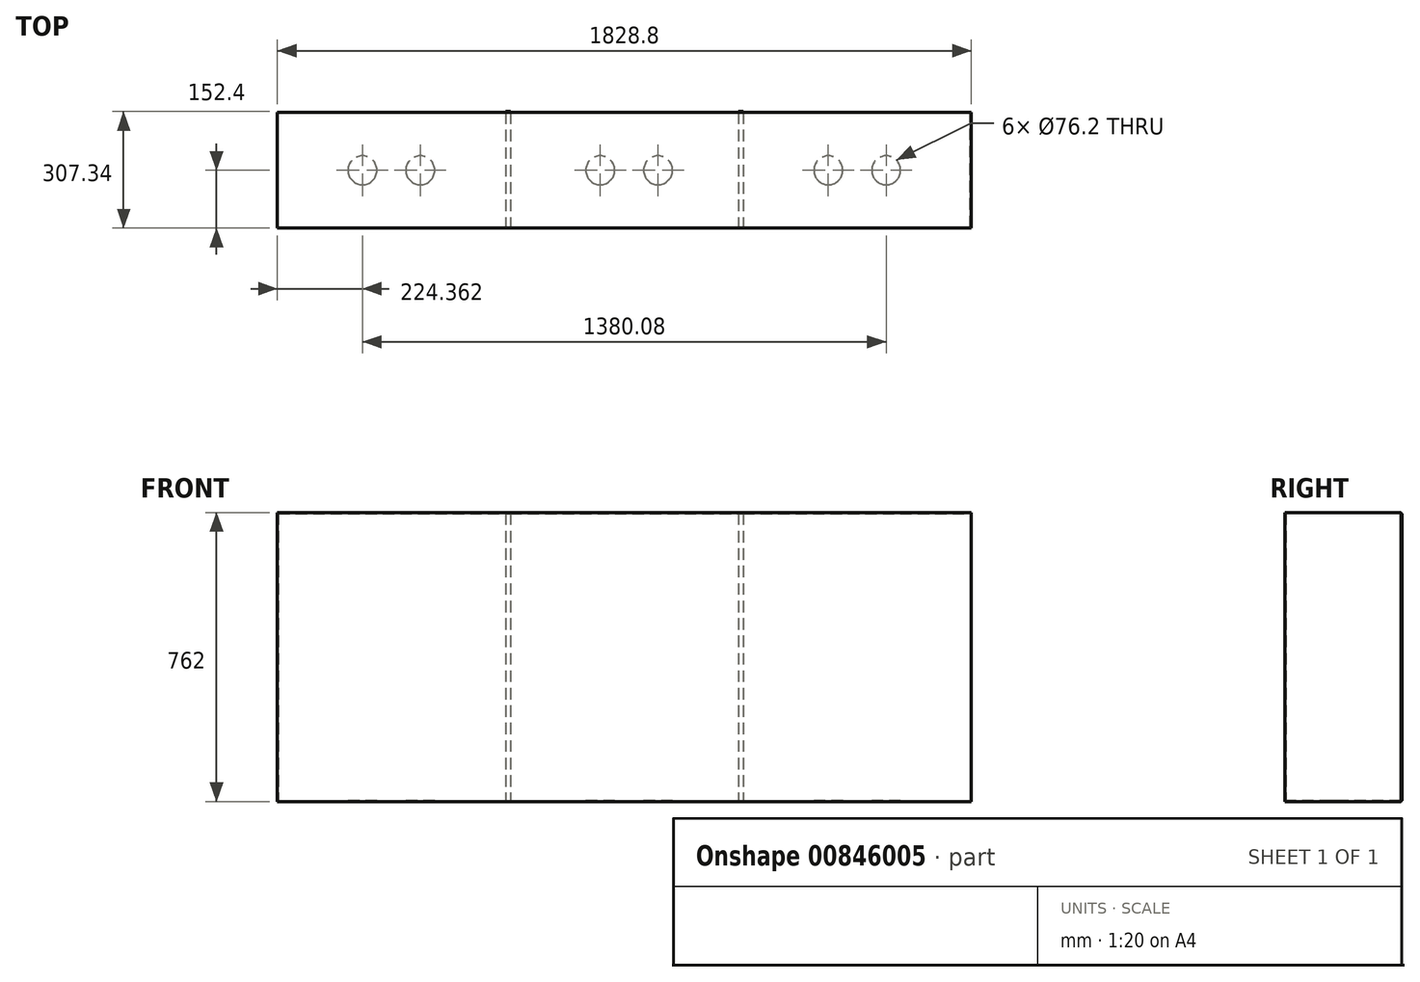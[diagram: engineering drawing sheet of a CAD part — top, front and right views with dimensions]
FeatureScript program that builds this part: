
annotation { "Feature Type Name" : "Feature", "Feature Type Description" : "" }
export const myFeature = defineFeature(function(context is Context, id is Id, definition is map)
    precondition{}
    {
        {
            var Q0;
            Q0=qCreatedBy(makeId("Front.planeOp"),FACE);
            var sketch = newSketch(context, id + "F0", { "sketchPlane" : qUnion([Q0])});
            skLineSegment(sketch, "E0.bottom", {"start": v(-461.04, 389.73) * mm, "end": v(1367.76, 389.73) * mm});
            skLineSegment(sketch, "E0.top", {"start": v(-461.04, -372.27) * mm, "end": v(1367.76, -372.27) * mm});
            skLineSegment(sketch, "E0.left", {"start": v(-461.04, 389.73) * mm, "end": v(-461.04, -372.27) * mm});
            skLineSegment(sketch, "E0.right", {"start": v(1367.76, 389.73) * mm, "end": v(1367.76, -372.27) * mm});
            skSolve(sketch);
        }
        {
            var Q0;
            Q0 = qSketchRegion(id + "F0", true);
            extrude(context, id + "F1", {"entities" : qUnion([Q0]), "depth" : 304.8 * mm, "offsetDistance" : 25.4 * mm});
        }
        {
            var Q0;
            Q0=makeQuery(id+"F1.opExtrude","CAP_FACE",FACE,{"disambiguationData":[OSD([sQuery(id+"F0.wireOp",EDGE,"E0.bottom"),sQuery(id+"F0.wireOp",EDGE,"E0.top"),sQuery(id+"F0.wireOp",EDGE,"E0.left"),sQuery(id+"F0.wireOp",EDGE,"E0.right")])],"isStart":true});
            shell(context, id + "F2", {"entities" : qUnion([Q0]), "thickness" : 2.54 * mm});
        }
        {
            var Q0;
            Q0=makeQuery(id+"F1.opExtrude","SWEPT_FACE",FACE,{"disambiguationData":[OSD([sQuery(id+"F0.wireOp",EDGE,"E0.top")])]});
            var sketch = newSketch(context, id + "F3", { "sketchPlane" : qUnion([Q0])});
            skLineSegment(sketch, "E1", {"start": v(-461.04, 152.4) * mm, "end": v(1367.76, 152.4) * mm});
            skLineSegment(sketch, "E2", {"start": v(165.51, 304.8) * mm, "end": v(165.51, 0) * mm});
            skLineSegment(sketch, "E3", {"start": v(766.65, 304.8) * mm, "end": v(766.65, 0) * mm});
            skCircle(sketch, "E4", {"center": v(-236.68, 152.4) * mm, "radius": 38.1 * mm});
            skCircle(sketch, "E5", {"center": v(-84.28, 152.4) * mm, "radius": 38.1 * mm});
            skCircle(sketch, "E6", {"center": v(389.87, 152.4) * mm, "radius": 38.1 * mm});
            skCircle(sketch, "E7", {"center": v(542.27, 152.4) * mm, "radius": 38.1 * mm});
            skCircle(sketch, "E8", {"center": v(991, 152.4) * mm, "radius": 38.1 * mm});
            skCircle(sketch, "E9", {"center": v(1143.4, 152.4) * mm, "radius": 38.1 * mm});
            skSolve(sketch);
        }
        {
            var Q0;
            Q0=sQuery(id+"F3.wireOp",VERTEX,"E4.center");
            var Q1;
            Q1=sQuery(id+"F3.wireOp",VERTEX,"E5.center");
            var Q2;
            Q2=sQuery(id+"F3.wireOp",VERTEX,"E6.center");
            var Q3;
            Q3=sQuery(id+"F3.wireOp",VERTEX,"E7.center");
            var Q4;
            Q4=sQuery(id+"F3.wireOp",VERTEX,"E8.center");
            var Q5;
            Q5=sQuery(id+"F3.wireOp",VERTEX,"E9.center");
            var Q6;
            Q6=makeQuery(id+"F1.opExtrude","SWEPT_BODY",BODY,{"disambiguationData":[OSD([sQuery(id+"F0.wireOp",EDGE,"E0.bottom"),sQuery(id+"F0.wireOp",EDGE,"E0.top"),sQuery(id+"F0.wireOp",EDGE,"E0.left"),sQuery(id+"F0.wireOp",EDGE,"E0.right")])]});
            hole(context, id + "F4", {"style" : HoleStyle.SIMPLE, "endStyle" : HoleEndStyle.BLIND, "holeDiameter" : 76.2 * mm, "majorDiameter" : 6.35 * mm, "holeDepth" : 12.7 * mm, "isTappedThrough" : true, "tappedDepth" : 12.7 * mm, "tapClearance" : 3, "locations" : qUnion([Q0, Q1, Q2, Q3, Q4, Q5]), "scope" : qUnion([Q6])});
        }
        {
            var Q0;
            Q0=makeQuery(id+"F2.opShell","OFFSET_FACE",FACE,{"disambiguationData":[OSD([sQuery(id+"F0.wireOp",EDGE,"E0.bottom"),sQuery(id+"F0.wireOp",EDGE,"E0.top"),sQuery(id+"F0.wireOp",EDGE,"E0.left"),sQuery(id+"F0.wireOp",EDGE,"E0.right")])]});
            var sketch = newSketch(context, id + "F5", { "sketchPlane" : qUnion([Q0])});
            skLineSegment(sketch, "E10.bottom", {"start": v(-766.64, 387.19) * mm, "end": v(-753.94, 387.19) * mm});
            skLineSegment(sketch, "E10.top", {"start": v(-766.64, -369.73) * mm, "end": v(-753.94, -369.73) * mm});
            skLineSegment(sketch, "E10.left", {"start": v(-766.64, 387.19) * mm, "end": v(-766.64, -369.73) * mm});
            skLineSegment(sketch, "E10.right", {"start": v(-753.94, 387.19) * mm, "end": v(-753.94, -369.73) * mm});
            skLineSegment(sketch, "E11.bottom", {"start": v(-152.8, 387.19) * mm, "end": v(-140.1, 387.19) * mm});
            skLineSegment(sketch, "E11.top", {"start": v(-152.8, -369.73) * mm, "end": v(-140.1, -369.73) * mm});
            skLineSegment(sketch, "E11.left", {"start": v(-152.8, 387.19) * mm, "end": v(-152.8, -369.73) * mm});
            skLineSegment(sketch, "E11.right", {"start": v(-140.1, 387.19) * mm, "end": v(-140.1, -369.73) * mm});
            skSolve(sketch);
        }
        {
            var Q0;
            Q0=makeQuery(id+"F5.imprint","IMPRINT",FACE,{"disambiguationData":[TD([[makeQuery(id+"F5.imprint","IMPRINT",EDGE,{"derivedFrom":sQuery(id+"F5.wireOp",EDGE,"E10.bottom")}),1.0]])]});
            var Q1;
            Q1=makeQuery(id+"F5.imprint","IMPRINT",FACE,{"disambiguationData":[TD([[makeQuery(id+"F5.imprint","IMPRINT",EDGE,{"derivedFrom":sQuery(id+"F5.wireOp",EDGE,"E11.bottom")}),1.0]])]});
            extrude(context, id + "F6", {"entities" : qUnion([Q0, Q1]), "operationType" : NewBodyOperationType.ADD, "depth" : 304.8 * mm, "offsetDistance" : 25.4 * mm});
        }
    });
